# Revit family: Electrical_Equipment-Network-Leviton-MetalSME
name_source: partatom
category: Electrical Equipment
revit_build: Autodesk Revit 2016 (Build: 20150506_1715(x64)
units: mm (PartAtom-declared; Revit-internal decimal feet)

## family parameters
Always vertical = Yes
Cut with Voids When Loaded = Yes
Host = Wall
Part Type = Other Panel
Room Calculation Point = No
Round Connector Dimension = Use Diameter
Shared = No

## types (3) — shared parameters
Check for Latest Version = leviton.com/bim
Date Last Modified = March 30, 2017
Equipment Abbreviation = MSME
Family Version = 1.0.0
Is Provided by Others = No
Manufacturer = Leviton
Model = See Product Page
Model Disclaimer = http://www.leviton.com
Product Page = http://www.leviton.com
URL = http://www.leviton.com
Width = 15.62 "

## per-type parameters (varying)
| type | Description | Height | z Leviton Type |
| 14" | Structured Media Enclosure, 14 in. | 15.35 " | 0 |
| 28" | Structured Media Enclosure, 28 in. | 28.1 " | 1 |
| 42" | Structured Media Enclosure, 42 in. | 42.1 " | 2 |

## geometry (parser evidence)
native form markers: Blend x8, Sweep x1
no freeform markers — native parametric forms only
